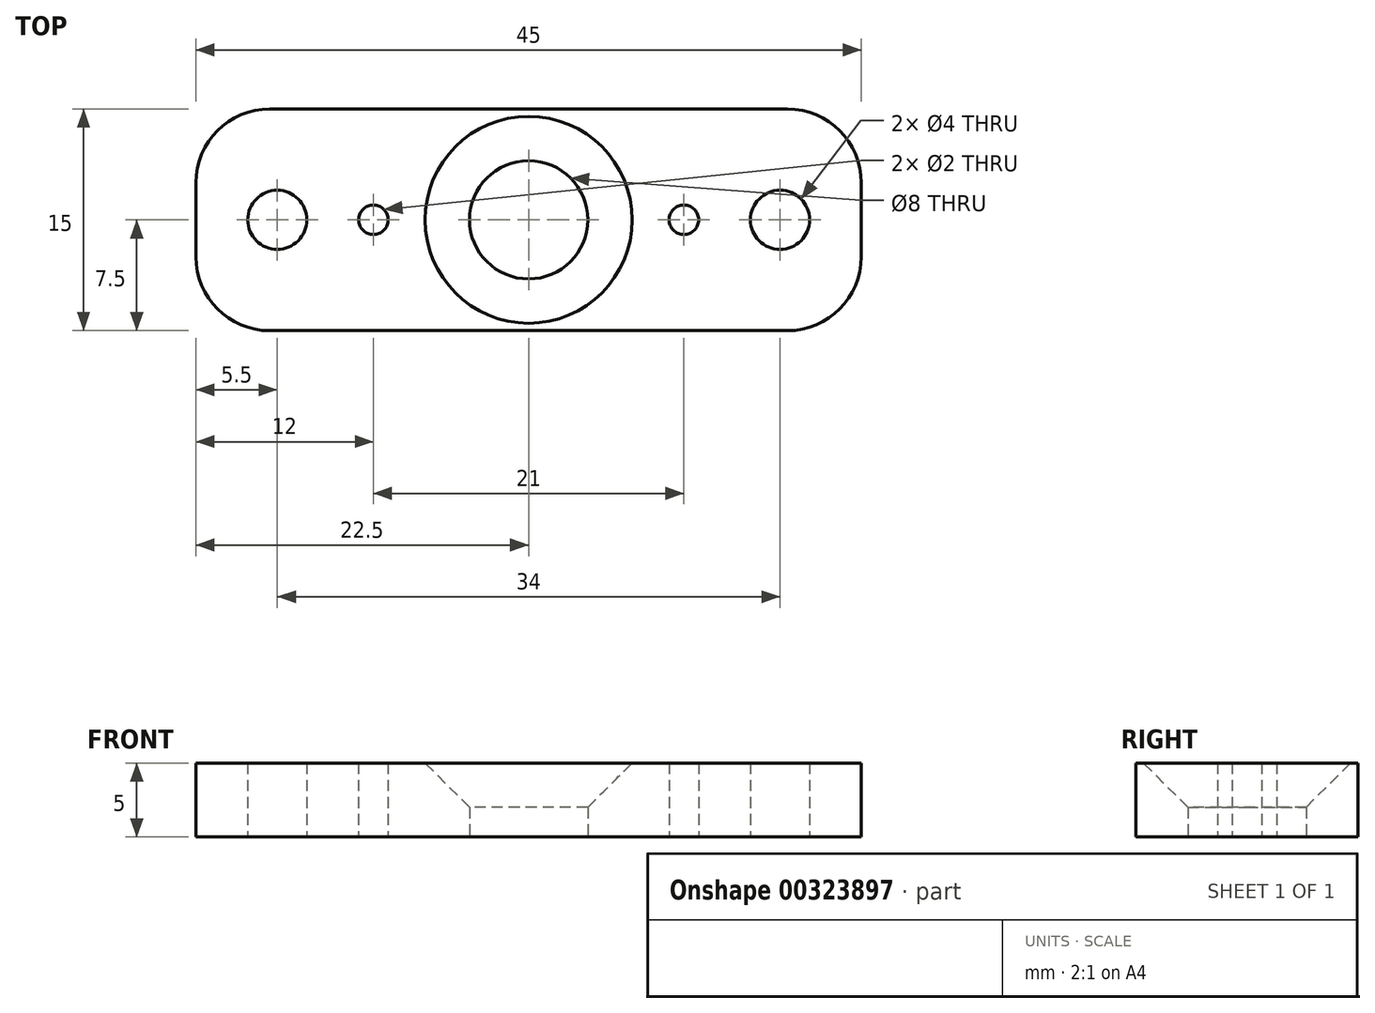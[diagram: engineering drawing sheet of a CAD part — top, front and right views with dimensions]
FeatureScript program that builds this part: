
annotation { "Feature Type Name" : "Feature", "Feature Type Description" : "" }
export const myFeature = defineFeature(function(context is Context, id is Id, definition is map)
    precondition{}
    {
        {
            var Q0;
            Q0=qCreatedBy(makeId("Top.planeOp"),FACE);
            var sketch = newSketch(context, id + "F0", { "sketchPlane" : qUnion([Q0])});
            skLineSegment(sketch, "E0.bottom", {"start": v(5, 0) * mm, "end": v(40, 0) * mm});
            skLineSegment(sketch, "E0.top", {"start": v(5, -15) * mm, "end": v(40, -15) * mm});
            skLineSegment(sketch, "E0.left", {"start": v(0, -5) * mm, "end": v(0, -10) * mm});
            skLineSegment(sketch, "E0.right", {"start": v(45, -5) * mm, "end": v(45, -10) * mm});
            skLineSegment(sketch, "E1", {"start": v(0, -7.5) * mm, "end": v(45, -7.5) * mm, "construction": true});
            skCircle(sketch, "E2", {"center": v(22.5, -7.5) * mm, "radius": 4 * mm});
            skCircle(sketch, "E3", {"center": v(5.5, -7.5) * mm, "radius": 2 * mm});
            skCircle(sketch, "E4", {"center": v(12, -7.5) * mm, "radius": 1 * mm});
            skLineSegment(sketch, "E5", {"start": v(22.5, 0) * mm, "end": v(22.5, -15) * mm, "construction": true});
            skCircle(sketch, "E6.MirrorC", {"center": v(39.5, -7.5) * mm, "radius": 2 * mm});
            skCircle(sketch, "E7.MirrorC", {"center": v(33, -7.5) * mm, "radius": 1 * mm});
            skPoint(sketch, "E8.visualSharp", {"position": v(0, 0) * mm});
            skArc(sketch, "E8.filletArc", {"start": v(5, 0) * mm, "mid": v(1.46, -1.46) * mm, "end": v(0, -5) * mm});
            skPoint(sketch, "E9.visualSharp", {"position": v(0, -15) * mm});
            skArc(sketch, "E9.filletArc", {"start": v(0, -10) * mm, "mid": v(1.46, -13.54) * mm, "end": v(5, -15) * mm});
            skPoint(sketch, "E10.visualSharp", {"position": v(45, 0) * mm});
            skArc(sketch, "E10.filletArc", {"start": v(45, -5) * mm, "mid": v(43.54, -1.46) * mm, "end": v(40, 0) * mm});
            skPoint(sketch, "E11.visualSharp", {"position": v(45, -15) * mm});
            skArc(sketch, "E11.filletArc", {"start": v(40, -15) * mm, "mid": v(43.54, -13.54) * mm, "end": v(45, -10) * mm});
            skSolve(sketch);
        }
        {
            var Q0;
            Q0=makeQuery(id+"F0.imprint","IMPRINT",FACE,{"disambiguationData":[TD([[makeQuery(id+"F0.imprint","IMPRINT",EDGE,{"derivedFrom":sQuery(id+"F0.wireOp",EDGE,"E0.bottom")}),-1.0]])]});
            extrude(context, id + "F1", {"entities" : qUnion([Q0]), "depth" : 5 * mm, "offsetDistance" : 25 * mm});
        }
        {
            var Q0;
            Q0=makeQuery(id+"F1.opExtrude","CAP_EDGE",EDGE,{"disambiguationData":[OSD([sQuery(id+"F0.wireOp",EDGE,"E2")])],"isStart":false});
            chamfer(context, id + "F2", {"entities" : qUnion([Q0]), "width" : 3 * mm, "tangentPropagation" : true});
        }
    });
